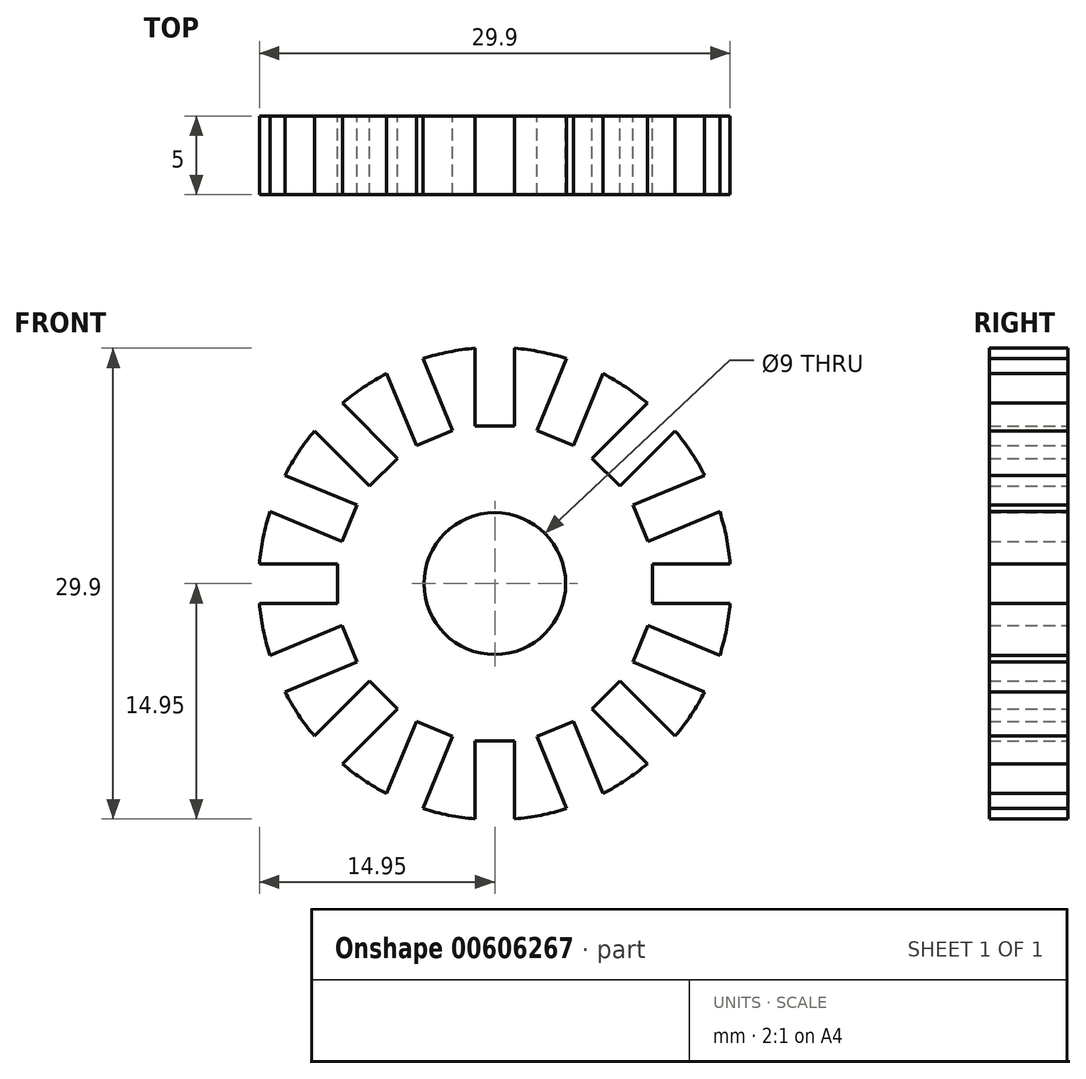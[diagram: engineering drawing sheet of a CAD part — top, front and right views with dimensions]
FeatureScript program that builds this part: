
annotation { "Feature Type Name" : "Feature", "Feature Type Description" : "" }
export const myFeature = defineFeature(function(context is Context, id is Id, definition is map)
    precondition{}
    {
        {
            var Q0;
            Q0=qCreatedBy(makeId("Front.planeOp"),FACE);
            var sketch = newSketch(context, id + "F0", { "sketchPlane" : qUnion([Q0])});
            skCircle(sketch, "E0", {"center": v(0, 0) * mm, "radius": 4.5 * mm});
            skCircle(sketch, "E1", {"center": v(0, 0) * mm, "radius": 15 * mm});
            skLineSegment(sketch, "E2.bottom", {"start": v(-1.25, 10) * mm, "end": v(1.25, 10) * mm});
            skLineSegment(sketch, "E2.top", {"start": v(-1.25, 20) * mm, "end": v(1.25, 20) * mm});
            skLineSegment(sketch, "E2.left", {"start": v(-1.25, 10) * mm, "end": v(-1.25, 20) * mm});
            skLineSegment(sketch, "E2.right", {"start": v(1.25, 10) * mm, "end": v(1.25, 20) * mm});
            skPoint(sketch, "E2.middle", {"position": v(0, 15) * mm});
            skLineSegment(sketch, "E3.1.0", {"start": v(-2.67, 9.72) * mm, "end": v(-6.5, 18.96) * mm});
            skLineSegment(sketch, "E3.1.1", {"start": v(-8.8, 18) * mm, "end": v(-6.5, 18.96) * mm});
            skLineSegment(sketch, "E3.1.2", {"start": v(-4.98, 8.76) * mm, "end": v(-8.8, 18) * mm});
            skLineSegment(sketch, "E3.1.3", {"start": v(-4.98, 8.76) * mm, "end": v(-2.67, 9.72) * mm});
            skLineSegment(sketch, "E3.2.0", {"start": v(-6.19, 7.95) * mm, "end": v(-13.26, 15.03) * mm});
            skLineSegment(sketch, "E3.2.1", {"start": v(-15.03, 13.26) * mm, "end": v(-13.26, 15.03) * mm});
            skLineSegment(sketch, "E3.2.2", {"start": v(-7.95, 6.19) * mm, "end": v(-15.03, 13.26) * mm});
            skLineSegment(sketch, "E3.2.3", {"start": v(-7.95, 6.19) * mm, "end": v(-6.19, 7.95) * mm});
            skLineSegment(sketch, "E4.1.3.0", {"start": v(-8.76, 4.98) * mm, "end": v(-18, 8.8) * mm});
            skLineSegment(sketch, "E4.3.3.0", {"start": v(-18.96, 6.5) * mm, "end": v(-18, 8.8) * mm});
            skLineSegment(sketch, "E4.6.3.0", {"start": v(-9.72, 2.67) * mm, "end": v(-18.96, 6.5) * mm});
            skLineSegment(sketch, "E4.9.3.0", {"start": v(-9.72, 2.67) * mm, "end": v(-8.76, 4.98) * mm});
            skLineSegment(sketch, "E4.1.4.0", {"start": v(-10, 1.25) * mm, "end": v(-20, 1.25) * mm});
            skLineSegment(sketch, "E4.3.4.0", {"start": v(-20, -1.25) * mm, "end": v(-20, 1.25) * mm});
            skLineSegment(sketch, "E4.6.4.0", {"start": v(-10, -1.25) * mm, "end": v(-20, -1.25) * mm});
            skLineSegment(sketch, "E4.9.4.0", {"start": v(-10, -1.25) * mm, "end": v(-10, 1.25) * mm});
            skLineSegment(sketch, "E4.1.5.0", {"start": v(-9.72, -2.67) * mm, "end": v(-18.96, -6.5) * mm});
            skLineSegment(sketch, "E4.3.5.0", {"start": v(-18, -8.8) * mm, "end": v(-18.96, -6.5) * mm});
            skLineSegment(sketch, "E4.6.5.0", {"start": v(-8.76, -4.98) * mm, "end": v(-18, -8.8) * mm});
            skLineSegment(sketch, "E4.9.5.0", {"start": v(-8.76, -4.98) * mm, "end": v(-9.72, -2.67) * mm});
            skLineSegment(sketch, "E4.1.6.0", {"start": v(-7.95, -6.19) * mm, "end": v(-15.03, -13.26) * mm});
            skLineSegment(sketch, "E4.3.6.0", {"start": v(-13.26, -15.03) * mm, "end": v(-15.03, -13.26) * mm});
            skLineSegment(sketch, "E4.6.6.0", {"start": v(-6.19, -7.95) * mm, "end": v(-13.26, -15.03) * mm});
            skLineSegment(sketch, "E4.9.6.0", {"start": v(-6.19, -7.95) * mm, "end": v(-7.95, -6.19) * mm});
            skLineSegment(sketch, "E4.1.7.0", {"start": v(-4.98, -8.76) * mm, "end": v(-8.8, -18) * mm});
            skLineSegment(sketch, "E4.3.7.0", {"start": v(-6.5, -18.96) * mm, "end": v(-8.8, -18) * mm});
            skLineSegment(sketch, "E4.6.7.0", {"start": v(-2.67, -9.72) * mm, "end": v(-6.5, -18.96) * mm});
            skLineSegment(sketch, "E4.9.7.0", {"start": v(-2.67, -9.72) * mm, "end": v(-4.98, -8.76) * mm});
            skLineSegment(sketch, "E4.1.8.0", {"start": v(-1.25, -10) * mm, "end": v(-1.25, -20) * mm});
            skLineSegment(sketch, "E4.3.8.0", {"start": v(1.25, -20) * mm, "end": v(-1.25, -20) * mm});
            skLineSegment(sketch, "E4.6.8.0", {"start": v(1.25, -10) * mm, "end": v(1.25, -20) * mm});
            skLineSegment(sketch, "E4.9.8.0", {"start": v(1.25, -10) * mm, "end": v(-1.25, -10) * mm});
            skLineSegment(sketch, "E4.1.9.0", {"start": v(2.67, -9.72) * mm, "end": v(6.5, -18.96) * mm});
            skLineSegment(sketch, "E4.3.9.0", {"start": v(8.8, -18) * mm, "end": v(6.5, -18.96) * mm});
            skLineSegment(sketch, "E4.6.9.0", {"start": v(4.98, -8.76) * mm, "end": v(8.8, -18) * mm});
            skLineSegment(sketch, "E4.9.9.0", {"start": v(4.98, -8.76) * mm, "end": v(2.67, -9.72) * mm});
            skLineSegment(sketch, "E4.1.10.0", {"start": v(6.19, -7.95) * mm, "end": v(13.26, -15.03) * mm});
            skLineSegment(sketch, "E4.3.10.0", {"start": v(15.03, -13.26) * mm, "end": v(13.26, -15.03) * mm});
            skLineSegment(sketch, "E4.6.10.0", {"start": v(7.95, -6.19) * mm, "end": v(15.03, -13.26) * mm});
            skLineSegment(sketch, "E4.9.10.0", {"start": v(7.95, -6.19) * mm, "end": v(6.19, -7.95) * mm});
            skLineSegment(sketch, "E4.1.11.0", {"start": v(8.76, -4.98) * mm, "end": v(18, -8.8) * mm});
            skLineSegment(sketch, "E4.3.11.0", {"start": v(18.96, -6.5) * mm, "end": v(18, -8.8) * mm});
            skLineSegment(sketch, "E4.6.11.0", {"start": v(9.72, -2.67) * mm, "end": v(18.96, -6.5) * mm});
            skLineSegment(sketch, "E4.9.11.0", {"start": v(9.72, -2.67) * mm, "end": v(8.76, -4.98) * mm});
            skLineSegment(sketch, "E4.1.12.0", {"start": v(10, -1.25) * mm, "end": v(20, -1.25) * mm});
            skLineSegment(sketch, "E4.3.12.0", {"start": v(20, 1.25) * mm, "end": v(20, -1.25) * mm});
            skLineSegment(sketch, "E4.6.12.0", {"start": v(10, 1.25) * mm, "end": v(20, 1.25) * mm});
            skLineSegment(sketch, "E4.9.12.0", {"start": v(10, 1.25) * mm, "end": v(10, -1.25) * mm});
            skLineSegment(sketch, "E4.1.13.0", {"start": v(9.72, 2.67) * mm, "end": v(18.96, 6.5) * mm});
            skLineSegment(sketch, "E4.3.13.0", {"start": v(18, 8.8) * mm, "end": v(18.96, 6.5) * mm});
            skLineSegment(sketch, "E4.6.13.0", {"start": v(8.76, 4.98) * mm, "end": v(18, 8.8) * mm});
            skLineSegment(sketch, "E4.9.13.0", {"start": v(8.76, 4.98) * mm, "end": v(9.72, 2.67) * mm});
            skLineSegment(sketch, "E4.1.14.0", {"start": v(7.95, 6.19) * mm, "end": v(15.03, 13.26) * mm});
            skLineSegment(sketch, "E4.3.14.0", {"start": v(13.26, 15.03) * mm, "end": v(15.03, 13.26) * mm});
            skLineSegment(sketch, "E4.6.14.0", {"start": v(6.19, 7.95) * mm, "end": v(13.26, 15.03) * mm});
            skLineSegment(sketch, "E4.9.14.0", {"start": v(6.19, 7.95) * mm, "end": v(7.95, 6.19) * mm});
            skLineSegment(sketch, "E4.1.15.0", {"start": v(4.98, 8.76) * mm, "end": v(8.8, 18) * mm});
            skLineSegment(sketch, "E4.3.15.0", {"start": v(6.5, 18.96) * mm, "end": v(8.8, 18) * mm});
            skLineSegment(sketch, "E4.6.15.0", {"start": v(2.67, 9.72) * mm, "end": v(6.5, 18.96) * mm});
            skLineSegment(sketch, "E4.9.15.0", {"start": v(2.67, 9.72) * mm, "end": v(4.98, 8.76) * mm});
            skSolve(sketch);
        }
        {
            var Q0;
            Q0=makeQuery(id+"F0.imprint","IMPRINT",FACE,{"disambiguationData":[TD([[makeQuery(id+"F0.imprint","IMPRINT",EDGE,{"derivedFrom":sQuery(id+"F0.wireOp",EDGE,"E0")}),-1.0]])]});
            extrude(context, id + "F1", {"entities" : qUnion([Q0]), "depth" : 5 * mm, "offsetDistance" : 25 * mm});
        }
    });
